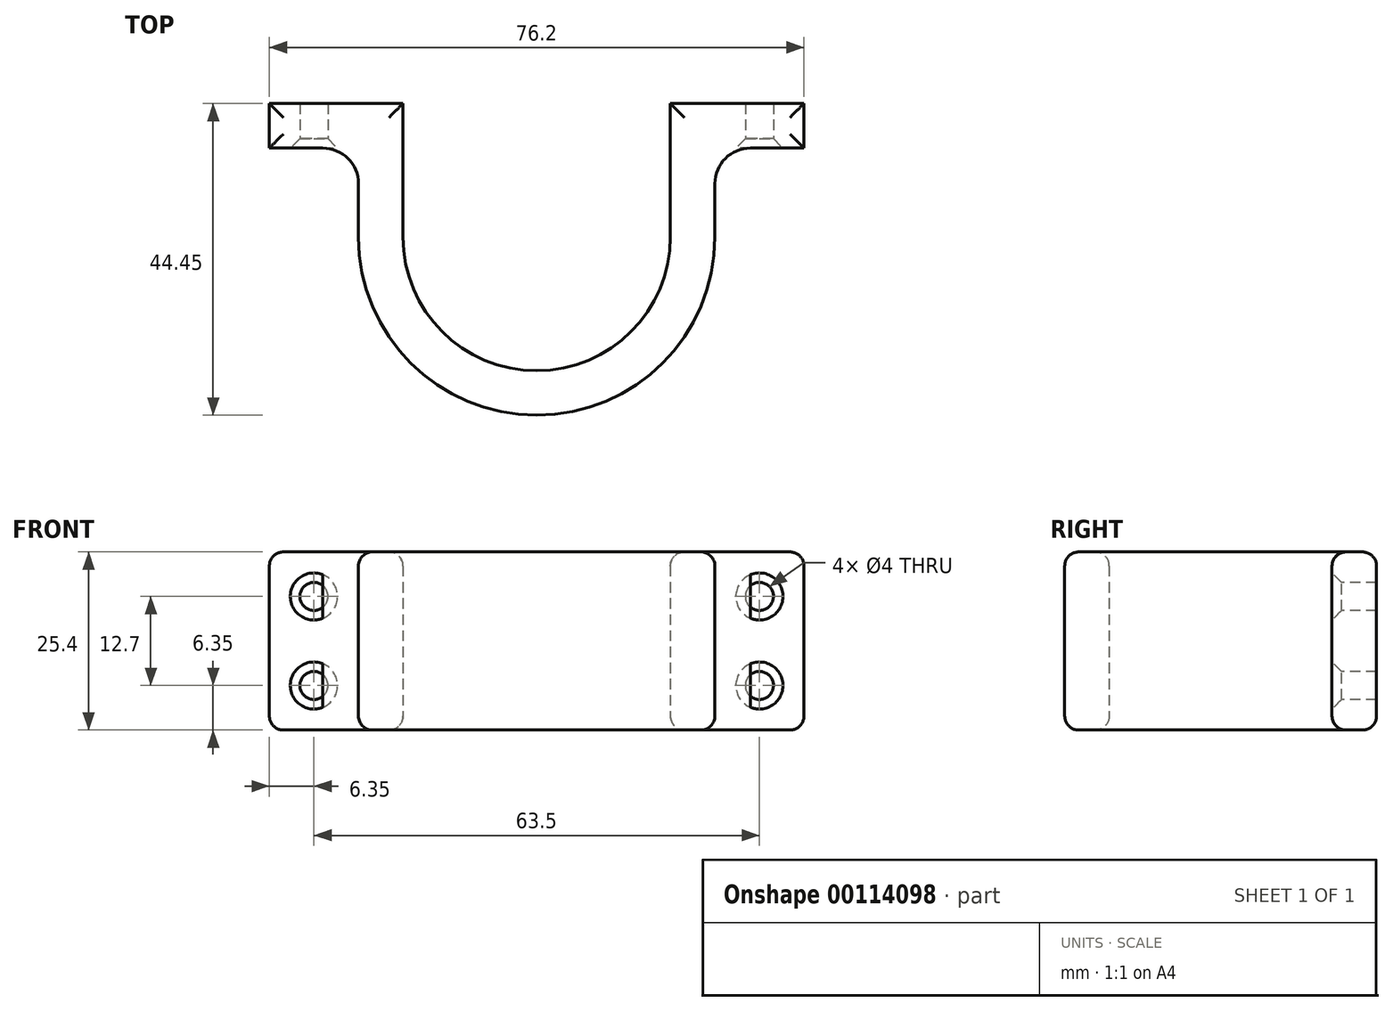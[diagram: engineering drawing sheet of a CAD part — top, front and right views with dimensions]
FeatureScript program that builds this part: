
annotation { "Feature Type Name" : "Feature", "Feature Type Description" : "" }
export const myFeature = defineFeature(function(context is Context, id is Id, definition is map)
    precondition{}
    {
        {
            var Q0;
            Q0=qCreatedBy(makeId("Top.planeOp"),FACE);
            var sketch = newSketch(context, id + "F0", { "sketchPlane" : qUnion([Q0])});
            skArc(sketch, "E0", {"start": v(19.05, 0) * mm, "mid": v(38.1, -19.05) * mm, "end": v(57.15, 0) * mm});
            skArc(sketch, "E1", {"start": v(12.7, 0) * mm, "mid": v(34.9, -25.2) * mm, "end": v(62.7, -6.35) * mm});
            skArc(sketch, "E2", {"start": v(12.7, 0) * mm, "mid": v(38.1, -25.4) * mm, "end": v(63.5, 0) * mm});
            skLineSegment(sketch, "E3.bottom", {"start": v(57.15, 19.05) * mm, "end": v(76.2, 19.05) * mm});
            skLineSegment(sketch, "E3.right", {"start": v(76.2, 19.05) * mm, "end": v(76.2, 12.7) * mm});
            skLineSegment(sketch, "E4.bottom", {"start": v(19.05, 19.05) * mm, "end": v(0, 19.05) * mm});
            skLineSegment(sketch, "E4.right", {"start": v(0, 19.05) * mm, "end": v(0, 12.7) * mm});
            skPoint(sketch, "E5.left.start.orphan", {"position": v(0, 0) * mm});
            skLineSegment(sketch, "E6", {"start": v(19.05, 0) * mm, "end": v(19.05, 19.05) * mm});
            skLineSegment(sketch, "E7", {"start": v(12.7, 0) * mm, "end": v(12.7, 12.7) * mm});
            skLineSegment(sketch, "E8", {"start": v(63.5, 0) * mm, "end": v(63.5, 12.7) * mm});
            skLineSegment(sketch, "E9", {"start": v(57.15, 0) * mm, "end": v(57.15, 19.05) * mm});
            skLineSegment(sketch, "E10.trimOffspring", {"start": v(12.7, 12.7) * mm, "end": v(0, 12.7) * mm});
            skLineSegment(sketch, "E11.trimOffspring", {"start": v(63.5, 12.7) * mm, "end": v(76.2, 12.7) * mm});
            skSolve(sketch);
        }
        {
            var Q0;
            Q0=makeQuery(id+"F0.imprint","IMPRINT",FACE,{"disambiguationData":[TD([[makeQuery(id+"F0.imprint","IMPRINT",EDGE,{"derivedFrom":sQuery(id+"F0.wireOp",EDGE,"E5.bottom")}),-1.0]])]});
            var Q1;
            Q1=makeQuery(id+"F0.imprint","IMPRINT",FACE,{"disambiguationData":[TD([[makeQuery(id+"F0.imprint","IMPRINT",EDGE,{"derivedFrom":sQuery(id+"F0.wireOp",EDGE,"E0")}),-1.0]])]});
            extrude(context, id + "F1", {"entities" : qUnion([Q0, Q1]), "depth" : 25.4 * mm});
        }
        {
            var Q0;
            Q0=makeQuery(id+"F1.opExtrude","SWEPT_EDGE",EDGE,{"disambiguationData":[OSD([sQuery(id+"F0.wireOp",EDGE,"E8"),sQuery(id+"F0.wireOp",EDGE,"E11.trimOffspring")])]});
            var Q1;
            Q1=makeQuery(id+"F1.opExtrude","SWEPT_EDGE",EDGE,{"disambiguationData":[OSD([sQuery(id+"F0.wireOp",EDGE,"E7"),sQuery(id+"F0.wireOp",EDGE,"E10.trimOffspring")])]});
            fillet(context, id + "F2", {"entities" : qUnion([Q0, Q1]), "radius" : 5.08 * mm, "tangentPropagation" : true, "allowEdgeOverflow" : false});
        }
        {
            var Q0;
            Q0=makeQuery(id+"F1.opExtrude","SWEPT_FACE",FACE,{"disambiguationData":[OSD([sQuery(id+"F0.wireOp",EDGE,"E11.trimOffspring")])]});
            var sketch = newSketch(context, id + "F3", { "sketchPlane" : qUnion([Q0])});
            skPoint(sketch, "E12", {"position": v(69.85, 19.05) * mm});
            skPoint(sketch, "E13", {"position": v(69.85, 6.35) * mm});
            skPoint(sketch, "E14", {"position": v(6.35, 6.35) * mm});
            skPoint(sketch, "E15", {"position": v(6.35, 19.05) * mm});
            skSolve(sketch);
        }
        {
            var Q0;
            Q0=sQuery(id+"F3.wireOp",VERTEX,"E15");
            var Q1;
            Q1=sQuery(id+"F3.wireOp",VERTEX,"E14");
            var Q2;
            Q2=sQuery(id+"F3.wireOp",VERTEX,"E12");
            var Q3;
            Q3=sQuery(id+"F3.wireOp",VERTEX,"E13");
            var Q4;
            Q4=makeQuery(id+"F1.opExtrude","SWEPT_BODY",BODY,{"disambiguationData":[OSD([sQuery(id+"F0.wireOp",EDGE,"E0"),sQuery(id+"F0.wireOp",EDGE,"E2"),sQuery(id+"F0.wireOp",EDGE,"E3.bottom"),sQuery(id+"F0.wireOp",EDGE,"E3.right"),sQuery(id+"F0.wireOp",EDGE,"E4.bottom"),sQuery(id+"F0.wireOp",EDGE,"E4.right"),sQuery(id+"F0.wireOp",EDGE,"E6"),sQuery(id+"F0.wireOp",EDGE,"E7"),sQuery(id+"F0.wireOp",EDGE,"E8"),sQuery(id+"F0.wireOp",EDGE,"E9"),sQuery(id+"F0.wireOp",EDGE,"E10.trimOffspring"),sQuery(id+"F0.wireOp",EDGE,"E11.trimOffspring")])]});
            hole(context, id + "F4", {"style" : HoleStyle.C_SINK, "endStyle" : HoleEndStyle.THROUGH, "holeDiameter" : 4 * mm, "cSinkDiameter" : 6.72 * mm, "cSinkAngle" : 90 * degree, "startFromSketch" : true, "locations" : qUnion([Q0, Q1, Q2, Q3]), "scope" : qUnion([Q4]), "isTappedThrough" : true});
        }
        {
            var Q0;
            Q0=makeQuery(id+"F1.opExtrude","CAP_FACE",FACE,{"disambiguationData":[OSD([sQuery(id+"F0.wireOp",EDGE,"E0"),sQuery(id+"F0.wireOp",EDGE,"E2"),sQuery(id+"F0.wireOp",EDGE,"E3.bottom"),sQuery(id+"F0.wireOp",EDGE,"E3.right"),sQuery(id+"F0.wireOp",EDGE,"E4.bottom"),sQuery(id+"F0.wireOp",EDGE,"E4.right"),sQuery(id+"F0.wireOp",EDGE,"E6"),sQuery(id+"F0.wireOp",EDGE,"E7"),sQuery(id+"F0.wireOp",EDGE,"E8"),sQuery(id+"F0.wireOp",EDGE,"E9"),sQuery(id+"F0.wireOp",EDGE,"E10.trimOffspring"),sQuery(id+"F0.wireOp",EDGE,"E11.trimOffspring")])],"isStart":false});
            var Q1;
            Q1=makeQuery(id+"F1.opExtrude","CAP_FACE",FACE,{"disambiguationData":[OSD([sQuery(id+"F0.wireOp",EDGE,"E0"),sQuery(id+"F0.wireOp",EDGE,"E2"),sQuery(id+"F0.wireOp",EDGE,"E3.bottom"),sQuery(id+"F0.wireOp",EDGE,"E3.right"),sQuery(id+"F0.wireOp",EDGE,"E4.bottom"),sQuery(id+"F0.wireOp",EDGE,"E4.right"),sQuery(id+"F0.wireOp",EDGE,"E6"),sQuery(id+"F0.wireOp",EDGE,"E7"),sQuery(id+"F0.wireOp",EDGE,"E8"),sQuery(id+"F0.wireOp",EDGE,"E9"),sQuery(id+"F0.wireOp",EDGE,"E10.trimOffspring"),sQuery(id+"F0.wireOp",EDGE,"E11.trimOffspring")])],"isStart":true});
            fillet(context, id + "F5", {"entities" : qUnion([Q0, Q1]), "radius" : 2 * mm, "tangentPropagation" : true, "allowEdgeOverflow" : false});
        }
    });
